# Revit family: Indoor_Floor Lamp_Santa&Cole_Cesta Outdoor
name_source: partatom
category: Luminarias
revit_build: Autodesk Revit 2018 (Build: 20170223_1515(x64)
units: mm (PartAtom-declared; Revit-internal decimal feet)

## family parameters
Compartido = No
Corte con vacíos al cargar = No
Cota de conector redondo = Diámetro de uso
Número OmniClass = 23.80.70.00
Origen de luz = Sí
Punto de cálculo de habitación = No
Se basa en plano de trabajo = No
Siempre vertical = Sí
Tipo de pieza = Normal
Título OmniClass = Lighting

## types (2) — shared parameters
Archivo de red fotométrica = CESTG01 (CL004A21F007G).IES
Assembly instructions - CE = https://www.santacole.com
Assembly instructions - UL = https://www.santacole.com
Cambio de temperatura de color de luz atenuada = <Ninguno>
Carga aparente = 12 VA
Descripción = EXTERIOR - Estructura de aluminio negro / verde oliva. Pantalla de polietileno blanco opal.
Fabricante = Santa & Cole
Filtro de color = 16777215
Load = 12 W
Manufacturer website = http://www.santacole.com
Modelo = Cesta Outdoor
Technical Information = https://www.santacole.com
URL = https://www.santacole.com
Ángulo de inclinación = -90.00°

## per-type parameters (varying)
| type | Code | Material |
| Cesta Outdoor - Negro | CESTF01 | Santa & Cole - Negro |
| Cesta Outdoor - Verde Oliva | CESTF02 | Santa & Cole - Verde Oliva |

## geometry (parser evidence)
native form markers: Sweep x2
no freeform markers — native parametric forms only
